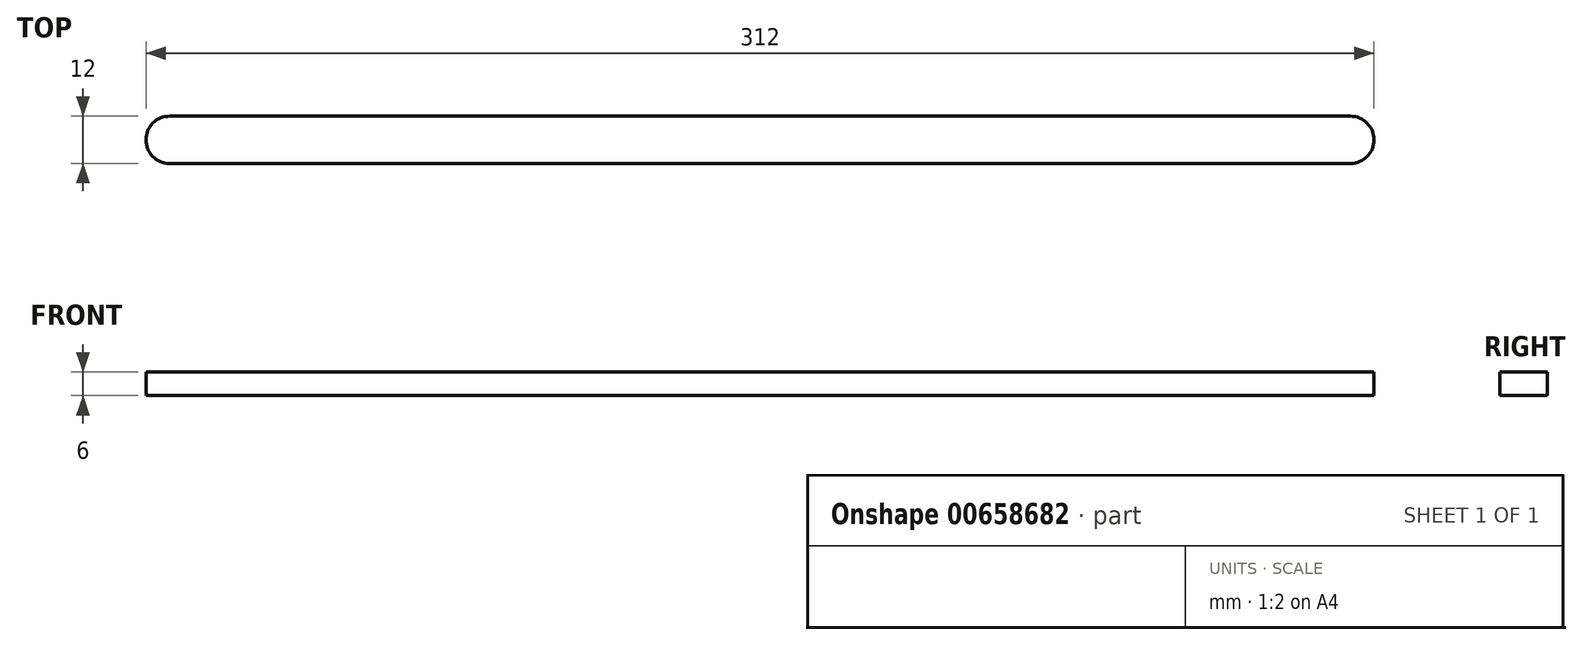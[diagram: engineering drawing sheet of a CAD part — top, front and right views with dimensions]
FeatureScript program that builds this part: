
annotation { "Feature Type Name" : "Feature", "Feature Type Description" : "" }
export const myFeature = defineFeature(function(context is Context, id is Id, definition is map)
    precondition{}
    {
        {
            var Q0;
            Q0=qCreatedBy(makeId("Top.planeOp"),FACE);
            var sketch = newSketch(context, id + "F0", { "sketchPlane" : qUnion([Q0])});
            skLineSegment(sketch, "E0", {"start": v(0, 0) * mm, "end": v(300, 0) * mm});
            skArc(sketch, "E1.0.startCap", {"start": v(0, -6) * mm, "mid": v(-6, 0) * mm, "end": v(0, 6) * mm});
            skArc(sketch, "E1.0.endCap", {"start": v(300, 6) * mm, "mid": v(306, 0) * mm, "end": v(300, -6) * mm});
            skLineSegment(sketch, "E1.0.left", {"start": v(0, 6) * mm, "end": v(300, 6) * mm});
            skLineSegment(sketch, "E1.0.right", {"start": v(0, -6) * mm, "end": v(300, -6) * mm});
            skLineSegment(sketch, "E2.0", {"start": v(0, 7) * mm, "end": v(300, 7) * mm});
            skArc(sketch, "E2.1", {"start": v(0, -7) * mm, "mid": v(-7, 0) * mm, "end": v(0, 7) * mm});
            skLineSegment(sketch, "E2.2", {"start": v(0, -7) * mm, "end": v(300, -7) * mm});
            skArc(sketch, "E2.3", {"start": v(300, 7) * mm, "mid": v(307, 0) * mm, "end": v(300, -7) * mm});
            skSolve(sketch);
        }
        {
            var Q0;
            Q0=makeQuery(id+"F0.imprint","IMPRINT",FACE,{"disambiguationData":[TD([[makeQuery(id+"F0.imprint","IMPRINT",EDGE,{"derivedFrom":sQuery(id+"F0.wireOp",EDGE,"E1.0.startCap")}),1.0]])]});
            extrude(context, id + "F1", {"entities" : qUnion([Q0]), "depth" : 6 * mm});
        }
    });
